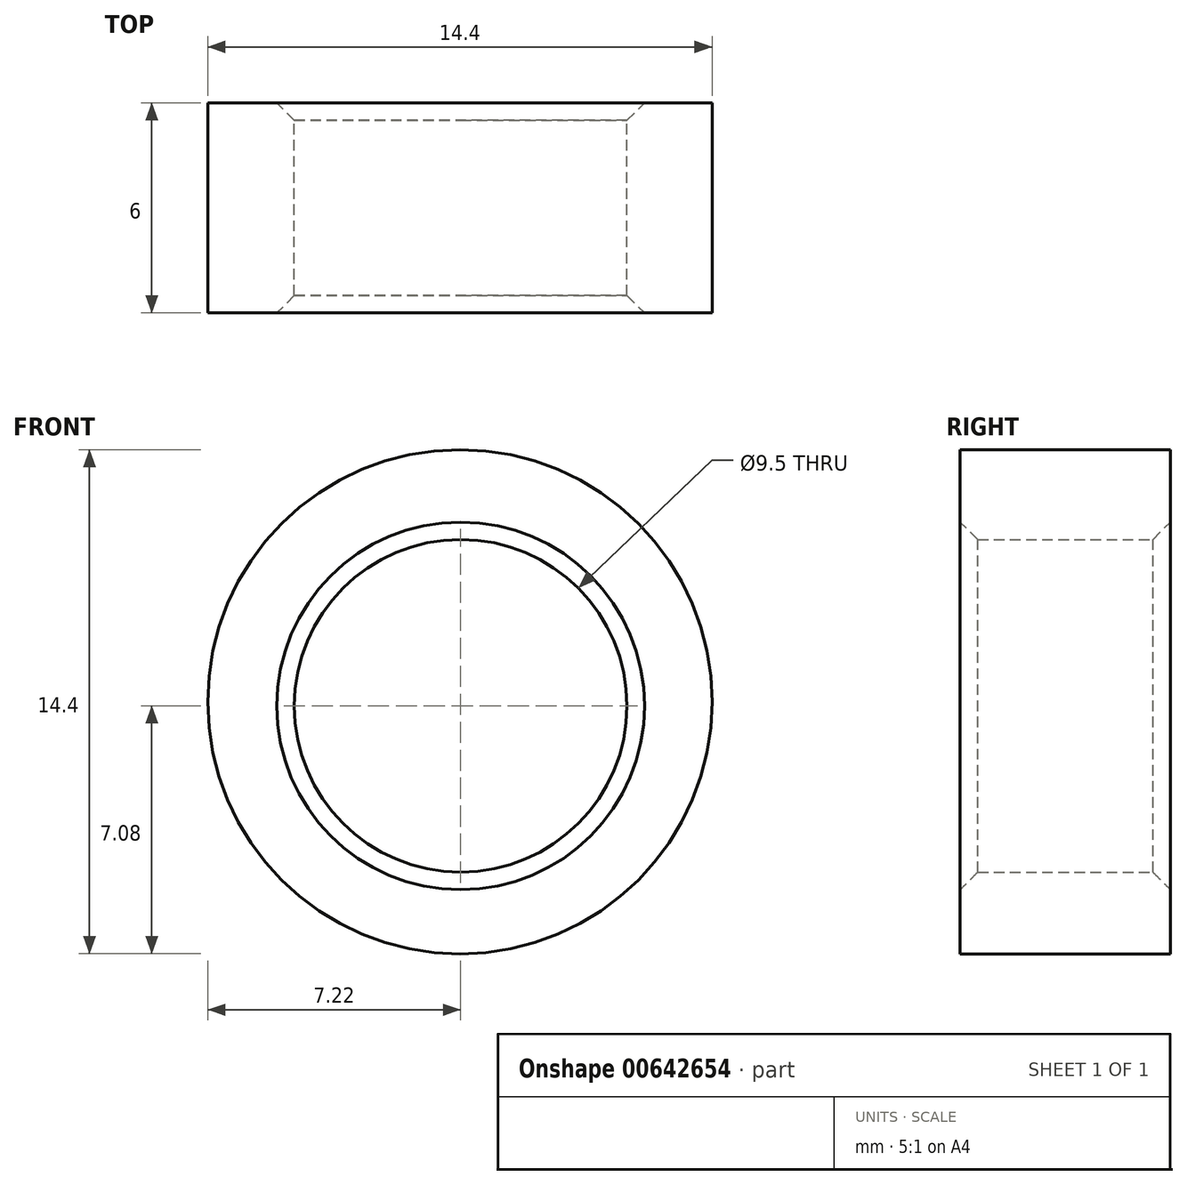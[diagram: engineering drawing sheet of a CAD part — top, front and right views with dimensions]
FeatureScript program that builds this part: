
annotation { "Feature Type Name" : "Feature", "Feature Type Description" : "" }
export const myFeature = defineFeature(function(context is Context, id is Id, definition is map)
    precondition{}
    {
        {
            var Q0;
            Q0=qCreatedBy(makeId("Front.planeOp"),FACE);
            var sketch = newSketch(context, id + "F0", { "sketchPlane" : qUnion([Q0])});
            skCircle(sketch, "E0", {"center": v(-0.02, 0.12) * mm, "radius": 7.2 * mm});
            skCircle(sketch, "E1", {"center": v(0, 0) * mm, "radius": 4.5 * mm});
            skCircle(sketch, "E2", {"center": v(0, 0) * mm, "radius": 4.75 * mm});
            skSolve(sketch);
        }
        {
            var Q0;
            Q0=makeQuery(id+"F0.imprint","IMPRINT",FACE,{"disambiguationData":[TD([[makeQuery(id+"F0.imprint","IMPRINT",EDGE,{"derivedFrom":sQuery(id+"F0.wireOp",EDGE,"E0")}),1.0]])]});
            var Q1;
            Q1=makeQuery(id+"F0.imprint","IMPRINT",FACE,{"disambiguationData":[TD([[makeQuery(id+"F0.imprint","IMPRINT",EDGE,{"derivedFrom":sQuery(id+"F0.wireOp",EDGE,"E1")}),1.0]])]});
            extrude(context, id + "F1", {"entities" : qUnion([Q0, Q1]), "depth" : 6 * mm, "offsetDistance" : 25.4 * mm});
        }
        {
            var Q0;
            Q0=makeQuery(id+"F1.opExtrude","CAP_FACE",FACE,{"disambiguationData":[OSD([sQuery(id+"F0.wireOp",EDGE,"E1")])],"isStart":false});
            extrude(context, id + "F2", {"entities" : qUnion([Q0]), "operationType" : NewBodyOperationType.REMOVE, "endBound" : BoundingType.THROUGH_ALL, "oppositeDirection" : true, "depth" : 25.4 * mm, "offsetDistance" : 25.4 * mm});
        }
        {
            var Q0;
            Q0=makeQuery(id+"F1.opExtrude","SWEPT_FACE",FACE,{"disambiguationData":[OSD([sQuery(id+"F0.wireOp",EDGE,"E2")])]});
            chamfer(context, id + "F3", {"entities" : qUnion([Q0]), "chamferType" : ChamferType.OFFSET_ANGLE, "width" : 0.5 * mm, "oppositeDirection" : false, "angle" : 45 * degree, "tangentPropagation" : true});
        }
    });
